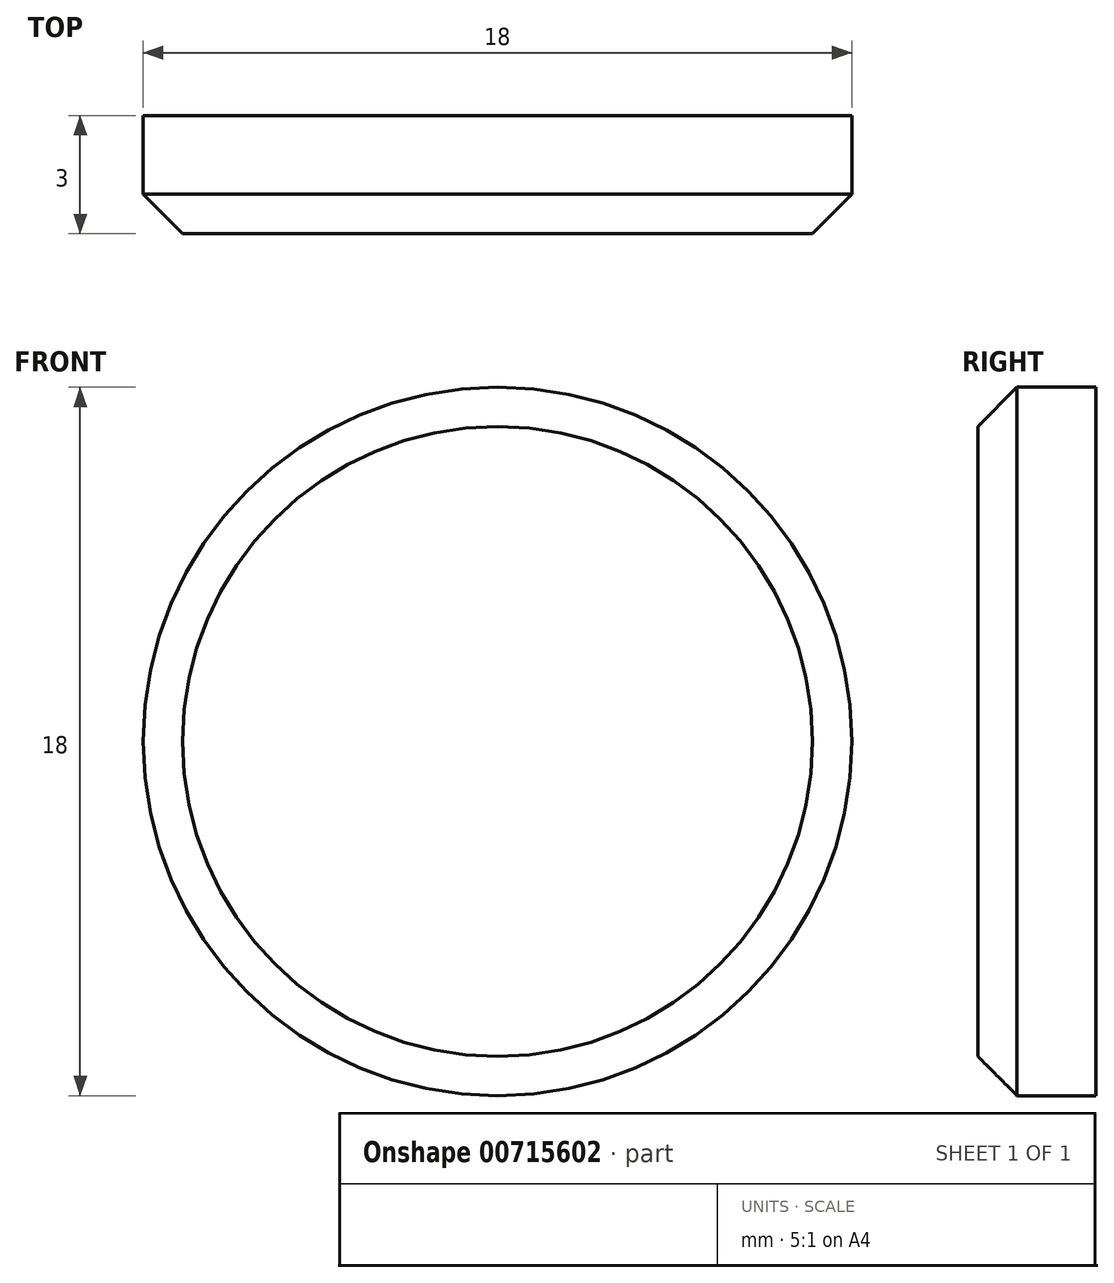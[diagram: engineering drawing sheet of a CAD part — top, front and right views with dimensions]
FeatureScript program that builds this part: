
annotation { "Feature Type Name" : "Feature", "Feature Type Description" : "" }
export const myFeature = defineFeature(function(context is Context, id is Id, definition is map)
    precondition{}
    {
        {
            var Q0;
            Q0=qCreatedBy(makeId("Front.planeOp"),FACE);
            var sketch = newSketch(context, id + "F0", { "sketchPlane" : qUnion([Q0])});
            skCircle(sketch, "E0", {"center": v(0, 0) * mm, "radius": 9 * mm});
            skSolve(sketch);
        }
        {
            var Q0;
            Q0 = qSketchRegion(id + "F0", true);
            extrude(context, id + "F1", {"entities" : qUnion([Q0]), "oppositeDirection" : true, "depth" : 3 * mm, "offsetDistance" : 25 * mm});
        }
        {
            var Q0;
            Q0=makeQuery(id+"F1.opExtrude","CAP_EDGE",EDGE,{"disambiguationData":[OSD([sQuery(id+"F0.wireOp",EDGE,"E0")])],"isStart":true});
            chamfer(context, id + "F2", {"entities" : qUnion([Q0]), "width" : 1 * mm, "tangentPropagation" : true});
        }
    });
